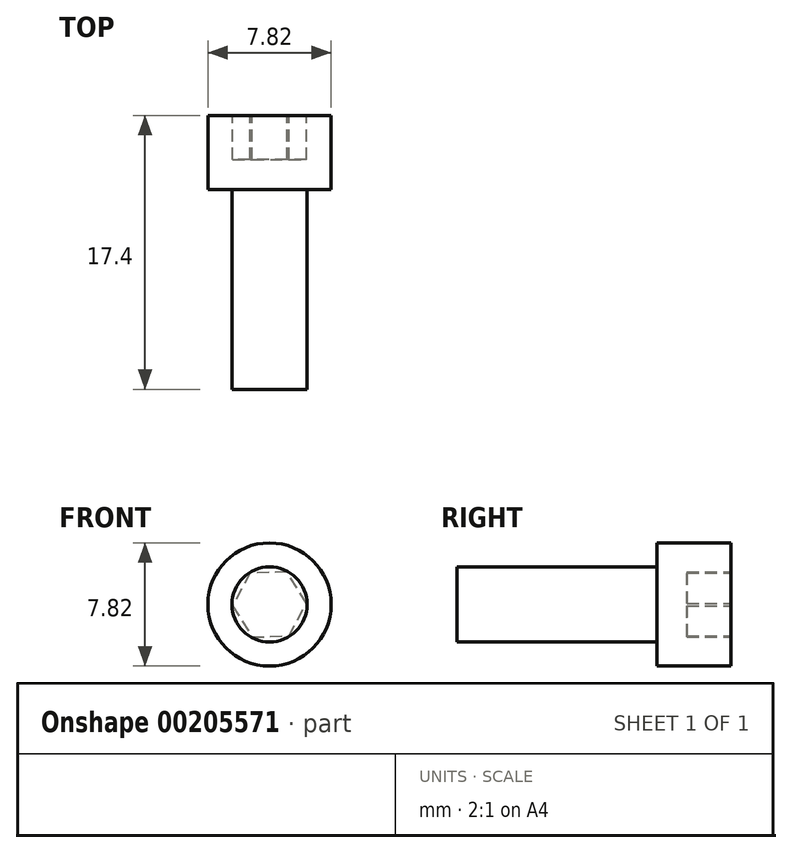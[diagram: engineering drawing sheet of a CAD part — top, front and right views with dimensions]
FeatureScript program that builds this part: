
annotation { "Feature Type Name" : "Feature", "Feature Type Description" : "" }
export const myFeature = defineFeature(function(context is Context, id is Id, definition is map)
    precondition{}
    {
        {
            var Q0;
            Q0=qCreatedBy(makeId("Front.planeOp"),FACE);
            var sketch = newSketch(context, id + "F0", { "sketchPlane" : qUnion([Q0])});
            skCircle(sketch, "E0", {"center": v(0, 0) * mm, "radius": 3.91 * mm});
            skSolve(sketch);
        }
        {
            var Q0;
            Q0=qSketchRegion(id+"F0",true);
            extrude(context, id + "F1", {"entities" : qUnion([Q0]), "oppositeDirection" : true, "depth" : 4.7 * mm});
        }
        {
            var Q0;
            Q0=makeQuery(id+"F1.opExtrude","CAP_FACE",FACE,{"disambiguationData":[OSD([sQuery(id+"F0.wireOp",EDGE,"E0")])],"isStart":true});
            var sketch = newSketch(context, id + "F2", { "sketchPlane" : qUnion([Q0])});
            skCircle(sketch, "E1", {"center": v(0, 0) * mm, "radius": 2.39 * mm});
            skSolve(sketch);
        }
        {
            var Q0;
            Q0=qSketchRegion(id+"F2",true);
            extrude(context, id + "F3", {"entities" : qUnion([Q0]), "operationType" : NewBodyOperationType.ADD, "depth" : 12.7 * mm});
        }
        {
            var Q0;
            Q0=makeQuery(id+"F1.opExtrude","CAP_FACE",FACE,{"disambiguationData":[OSD([sQuery(id+"F0.wireOp",EDGE,"E0")])],"isStart":false});
            var sketch = newSketch(context, id + "F4", { "sketchPlane" : qUnion([Q0])});
            skCircle(sketch, "E2.cCircle", {"center": v(0, 0) * mm, "radius": 2.03 * mm, "construction": true});
            skLineSegment(sketch, "E2.0", {"start": v(-1.24, -2) * mm, "end": v(-2.34, 0.08) * mm});
            skLineSegment(sketch, "E2.1", {"start": v(-2.34, 0.08) * mm, "end": v(-1.1, 2.07) * mm});
            skLineSegment(sketch, "E2.2", {"start": v(-1.1, 2.07) * mm, "end": v(1.24, 2) * mm});
            skLineSegment(sketch, "E2.3", {"start": v(1.24, 2) * mm, "end": v(2.34, -0.08) * mm});
            skLineSegment(sketch, "E2.4", {"start": v(2.34, -0.08) * mm, "end": v(1.1, -2.07) * mm});
            skLineSegment(sketch, "E2.5", {"start": v(1.1, -2.07) * mm, "end": v(-1.24, -2) * mm});
            skPoint(sketch, "E2.0.midPoint", {"position": v(-1.8, -0.95) * mm});
            skSolve(sketch);
        }
        {
            var Q0;
            Q0=qSketchRegion(id+"F4",true);
            extrude(context, id + "F5", {"entities" : qUnion([Q0]), "operationType" : NewBodyOperationType.REMOVE, "oppositeDirection" : true, "depth" : 2.8 * mm});
        }
    });
